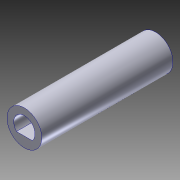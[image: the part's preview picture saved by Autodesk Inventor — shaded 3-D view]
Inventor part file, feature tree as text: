
AUTODESK INVENTOR PART (.ipt)
format: ipt  version: 2013 (Build 170138000, 138)  size: 93,696 bytes
history: native  units: mm
features: extrude x2, sketch x2, plane x1
ambient origin geometry x8: Origin, YZ Plane, XZ Plane, XY Plane, X Axis, Y Axis, Z Axis, Center Point
bodies: Solid1 (feature_tree)
feature tree (5):
  extrude  "Extrusion1"  Depth=4.9mm
  plane  "Work Plane1"
  extrude  "Extrusion6"  Depth=18.5mm TaperAngle=0.0deg
  sketch  "Sketch1"  dims[d0=3.0mm d1=4.9mm]
  sketch  "Sketch6"  dims[d2=0.5mm d4=18.5mm d5=0.0mm d20=4.0mm d21=6.0mm d22=5.0mm d23=0.5mm d24=0.0mm]
